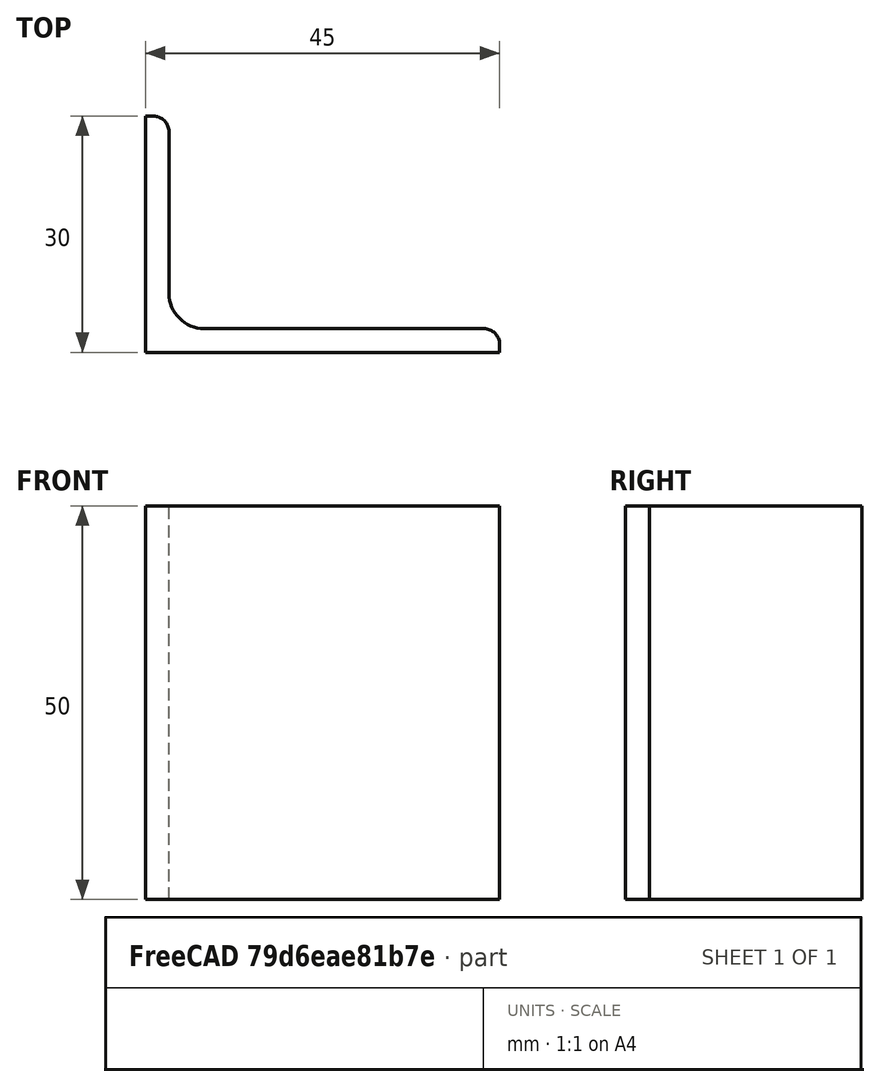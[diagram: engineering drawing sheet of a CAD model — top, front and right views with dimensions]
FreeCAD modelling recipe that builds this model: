
FCSTD DOCUMENT  (FreeCAD 0.15R4671 (Git))
Label: Angle Bar 45x30x3 EN10056 S235JR
License: All rights reserved
LicenseURL: http://en.wikipedia.org/wiki/All_rights_reserved
objects: Sketcher::SketchObject×1, Part::Extrusion×1
note: 2 computed .brp shape members not serialized (recipe doc carries the construction recipe); baked Part::Feature solids carry a one-line shape summary decoded from their .brp

FEATURE [Sketcher::SketchObject] Sketch
  sketch-geometry (9):
    g0: LineSegment StartX=0 StartY=0 StartZ=0 EndX=45 EndY=0 EndZ=0
    g1: LineSegment StartX=45 StartY=0 StartZ=0 EndX=45 EndY=1 EndZ=0
    g2: LineSegment StartX=43 StartY=3 StartZ=0 EndX=7.5 EndY=3 EndZ=0
    g3: LineSegment StartX=0 StartY=0 StartZ=0 EndX=0 EndY=30 EndZ=0
    g4: LineSegment StartX=0 StartY=30 StartZ=0 EndX=1 EndY=30 EndZ=0
    g5: LineSegment StartX=3 StartY=28 StartZ=0 EndX=3 EndY=7.5 EndZ=0
    g6: ArcOfCircle CenterX=7.5 CenterY=7.5 CenterZ=0 NormalX=0 NormalY=0 NormalZ=1 Radius=4.5 StartAngle=3.14159 EndAngle=4.71239
    g7: ArcOfCircle CenterX=1 CenterY=28 CenterZ=0 NormalX=0 NormalY=0 NormalZ=1 Radius=2 StartAngle=0 EndAngle=1.5708
    g8: ArcOfCircle CenterX=43 CenterY=1 CenterZ=0 NormalX=0 NormalY=0 NormalZ=1 Radius=2 StartAngle=0 EndAngle=1.5708
  constraints (23):
    c: Coincident(g0,g-1)
    c: Horizontal(g0)
    c: Coincident(g1,g0)
    c: Vertical(g1)
    c: Horizontal(g2)
    c: Coincident(g3,g-1)
    c: Vertical(g3)
    c: Coincident(g4,g3)
    c: Horizontal(g4)
    c: Vertical(g5)
    c: Tangent(g5,g6) = -1.5708
    c: Tangent(g2,g6) = 1.5708
    c: Tangent(g4,g7) = 1.5708
    c: Tangent(g5,g7) = 1.5708
    c: Tangent(g2,g8) = -1.5708
    c: Tangent(g1,g8) = -1.5708
    c: DistanceX(g0) = 45
    c: DistanceY(g3) = 30
    c: DistanceY(g0,g2) = 3
    c: DistanceX(g3,g5) = 3
    c: Radius(g6) = 4.5
    c: Radius(g8) = 2
    c: Radius(g7) = 2
FEATURE [Part::Extrusion] Extrude  label="Angle Bar 45x30x3 EN10056 S235JR"
  Base = -> Sketch
  Dir = (0,0,50)
  Solid = true
